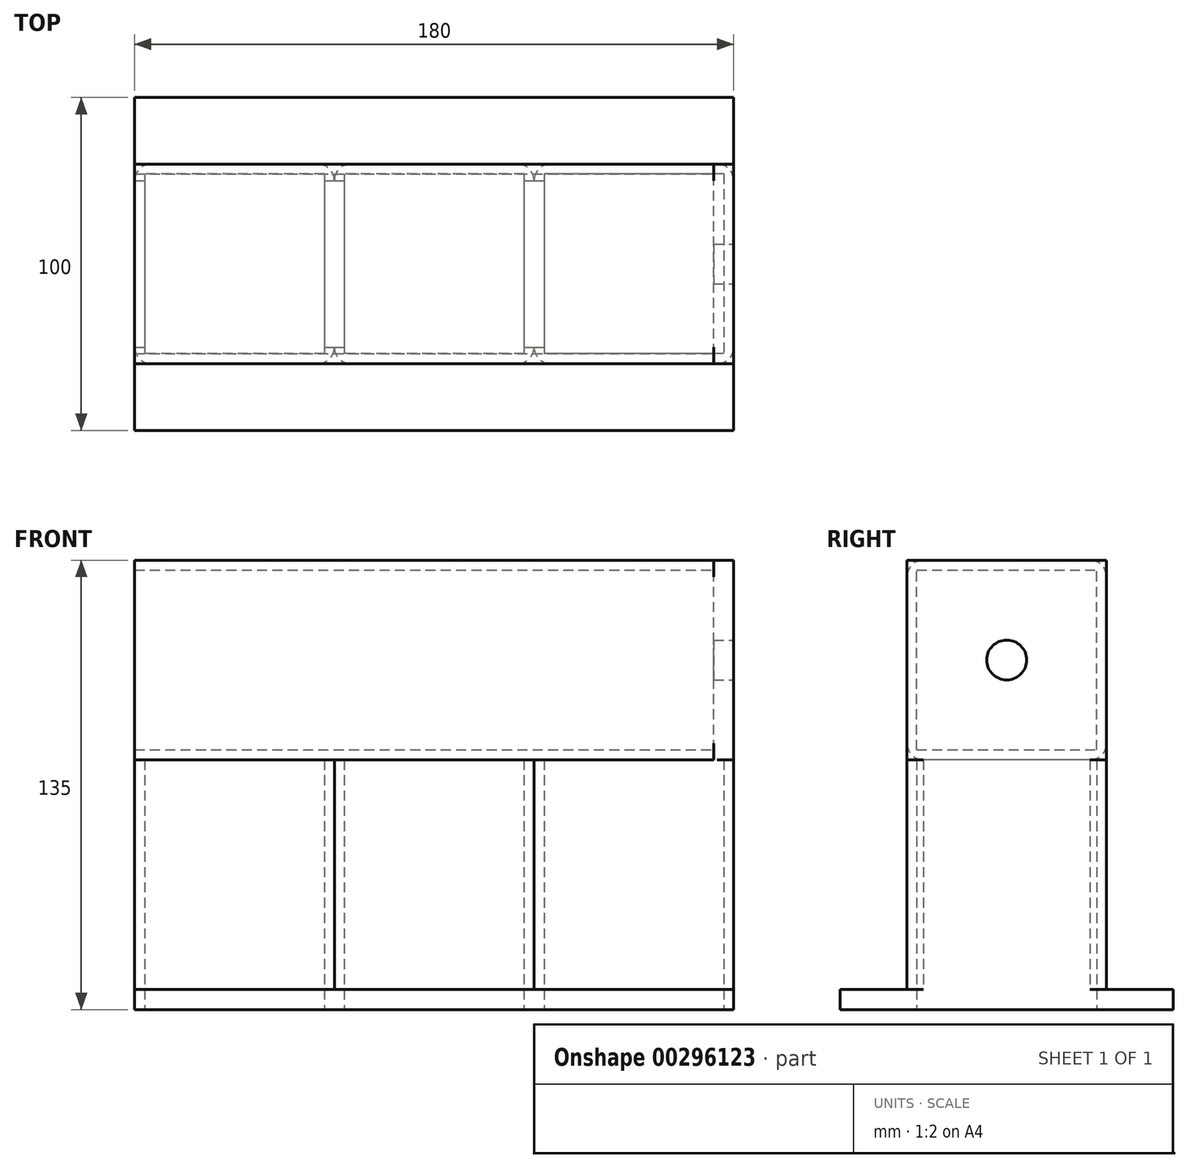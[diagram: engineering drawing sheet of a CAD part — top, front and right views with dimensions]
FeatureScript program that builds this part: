
annotation { "Feature Type Name" : "Feature", "Feature Type Description" : "" }
export const myFeature = defineFeature(function(context is Context, id is Id, definition is map)
    precondition{}
    {
        {
            var Q0;
            Q0=qCreatedBy(makeId("Top.planeOp"),FACE);
            var sketch = newSketch(context, id + "F0", { "sketchPlane" : qUnion([Q0])});
            skLineSegment(sketch, "E0.bottom", {"start": v(-15.85, -3.6) * mm, "end": v(-65.85, -3.6) * mm});
            skLineSegment(sketch, "E0.top", {"start": v(-15.85, -63.6) * mm, "end": v(-65.85, -63.6) * mm});
            skLineSegment(sketch, "E0.left", {"start": v(-10.85, -8.6) * mm, "end": v(-10.85, -58.6) * mm});
            skLineSegment(sketch, "E0.right", {"start": v(-70.85, -8.6) * mm, "end": v(-70.85, -58.6) * mm});
            skPoint(sketch, "E0.middle", {"position": v(-40.85, -33.6) * mm});
            skPoint(sketch, "E1.visualSharp", {"position": v(-70.85, -3.6) * mm});
            skArc(sketch, "E1.filletArc", {"start": v(-65.85, -3.6) * mm, "mid": v(-69.39, -5.06) * mm, "end": v(-70.85, -8.6) * mm});
            skPoint(sketch, "E2.visualSharp", {"position": v(-10.85, -3.6) * mm});
            skArc(sketch, "E2.filletArc", {"start": v(-10.85, -8.6) * mm, "mid": v(-12.31, -5.06) * mm, "end": v(-15.85, -3.6) * mm});
            skPoint(sketch, "E3.visualSharp", {"position": v(-10.85, -63.6) * mm});
            skArc(sketch, "E3.filletArc", {"start": v(-15.85, -63.6) * mm, "mid": v(-12.31, -62.13) * mm, "end": v(-10.85, -58.6) * mm});
            skPoint(sketch, "E4.visualSharp", {"position": v(-70.85, -63.6) * mm});
            skArc(sketch, "E4.filletArc", {"start": v(-70.85, -58.6) * mm, "mid": v(-69.39, -62.13) * mm, "end": v(-65.85, -63.6) * mm});
            skLineSegment(sketch, "E5.0", {"start": v(-67.85, -6.6) * mm, "end": v(-67.85, -60.6) * mm});
            skLineSegment(sketch, "E5.1", {"start": v(-13.85, -6.6) * mm, "end": v(-67.85, -6.6) * mm});
            skLineSegment(sketch, "E5.2", {"start": v(-13.85, -6.6) * mm, "end": v(-13.85, -60.6) * mm});
            skLineSegment(sketch, "E5.3", {"start": v(-13.85, -60.6) * mm, "end": v(-67.85, -60.6) * mm});
            skLineSegment(sketch, "E6.bottom", {"start": v(44.15, -3.6) * mm, "end": v(-5.85, -3.6) * mm});
            skLineSegment(sketch, "E6.top", {"start": v(44.15, -63.6) * mm, "end": v(-5.85, -63.6) * mm});
            skLineSegment(sketch, "E6.left", {"start": v(49.15, -8.6) * mm, "end": v(49.15, -58.6) * mm});
            skPoint(sketch, "E6.middle", {"position": v(19.15, -33.6) * mm});
            skArc(sketch, "E7.filletArc", {"start": v(-5.85, -3.6) * mm, "mid": v(-9.39, -5.06) * mm, "end": v(-10.85, -8.6) * mm});
            skPoint(sketch, "E8.visualSharp", {"position": v(49.15, -3.6) * mm});
            skArc(sketch, "E8.filletArc", {"start": v(49.15, -8.6) * mm, "mid": v(47.69, -5.06) * mm, "end": v(44.15, -3.6) * mm});
            skPoint(sketch, "E9.visualSharp", {"position": v(49.15, -63.6) * mm});
            skArc(sketch, "E9.filletArc", {"start": v(44.15, -63.6) * mm, "mid": v(47.69, -62.13) * mm, "end": v(49.15, -58.6) * mm});
            skArc(sketch, "E10.filletArc", {"start": v(-10.85, -58.6) * mm, "mid": v(-9.39, -62.13) * mm, "end": v(-5.85, -63.6) * mm});
            skLineSegment(sketch, "E11.0", {"start": v(-7.85, -6.6) * mm, "end": v(-7.85, -60.6) * mm});
            skLineSegment(sketch, "E11.1", {"start": v(46.15, -6.6) * mm, "end": v(-7.85, -6.6) * mm});
            skLineSegment(sketch, "E11.2", {"start": v(46.15, -6.6) * mm, "end": v(46.15, -60.6) * mm});
            skLineSegment(sketch, "E11.3", {"start": v(46.15, -60.6) * mm, "end": v(-7.85, -60.6) * mm});
            skLineSegment(sketch, "E12.bottom", {"start": v(104.15, -3.6) * mm, "end": v(54.15, -3.6) * mm});
            skLineSegment(sketch, "E12.top", {"start": v(104.15, -63.6) * mm, "end": v(54.15, -63.6) * mm});
            skLineSegment(sketch, "E12.left", {"start": v(109.15, -8.6) * mm, "end": v(109.15, -58.6) * mm});
            skPoint(sketch, "E12.middle", {"position": v(79.15, -33.6) * mm});
            skArc(sketch, "E13.filletArc", {"start": v(54.15, -3.6) * mm, "mid": v(50.61, -5.06) * mm, "end": v(49.15, -8.6) * mm});
            skPoint(sketch, "E14.visualSharp", {"position": v(109.15, -3.6) * mm});
            skArc(sketch, "E14.filletArc", {"start": v(109.15, -8.6) * mm, "mid": v(107.69, -5.06) * mm, "end": v(104.15, -3.6) * mm});
            skPoint(sketch, "E15.visualSharp", {"position": v(109.15, -63.6) * mm});
            skArc(sketch, "E15.filletArc", {"start": v(104.15, -63.6) * mm, "mid": v(107.69, -62.13) * mm, "end": v(109.15, -58.6) * mm});
            skArc(sketch, "E16.filletArc", {"start": v(49.15, -58.6) * mm, "mid": v(50.61, -62.13) * mm, "end": v(54.15, -63.6) * mm});
            skLineSegment(sketch, "E17.0", {"start": v(52.15, -6.6) * mm, "end": v(52.15, -60.6) * mm});
            skLineSegment(sketch, "E17.1", {"start": v(106.15, -6.6) * mm, "end": v(52.15, -6.6) * mm});
            skLineSegment(sketch, "E17.2", {"start": v(106.15, -6.6) * mm, "end": v(106.15, -60.6) * mm});
            skLineSegment(sketch, "E17.3", {"start": v(106.15, -60.6) * mm, "end": v(52.15, -60.6) * mm});
            skSolve(sketch);
        }
        {
            var Q0;
            Q0=makeQuery(id+"F0.imprint","IMPRINT",FACE,{"disambiguationData":[TD([[makeQuery(id+"F0.imprint","IMPRINT",EDGE,{"derivedFrom":sQuery(id+"F0.wireOp",EDGE,"E0.bottom")}),1.0]])]});
            var Q1;
            Q1=makeQuery(id+"F0.imprint","IMPRINT",FACE,{"disambiguationData":[TD([[makeQuery(id+"F0.imprint","IMPRINT",EDGE,{"derivedFrom":sQuery(id+"F0.wireOp",EDGE,"E6.bottom")}),1.0]])]});
            var Q2;
            Q2=makeQuery(id+"F0.imprint","IMPRINT",FACE,{"disambiguationData":[TD([[makeQuery(id+"F0.imprint","IMPRINT",EDGE,{"derivedFrom":sQuery(id+"F0.wireOp",EDGE,"E12.bottom")}),1.0]])]});
            extrude(context, id + "F1", {"entities" : qUnion([Q0, Q1, Q2]), "depth" : 69 * mm});
        }
        {
            var Q0;
            Q0=makeQuery(id+"F1.opExtrude","CAP_FACE",FACE,{"disambiguationData":[OSD([sQuery(id+"F0.wireOp",EDGE,"E0.bottom"),sQuery(id+"F0.wireOp",EDGE,"E0.top"),sQuery(id+"F0.wireOp",EDGE,"E0.right"),sQuery(id+"F0.wireOp",EDGE,"E1.filletArc"),sQuery(id+"F0.wireOp",EDGE,"E2.filletArc"),sQuery(id+"F0.wireOp",EDGE,"E3.filletArc"),sQuery(id+"F0.wireOp",EDGE,"E4.filletArc"),sQuery(id+"F0.wireOp",EDGE,"E5.0"),sQuery(id+"F0.wireOp",EDGE,"E5.1"),sQuery(id+"F0.wireOp",EDGE,"E5.2"),sQuery(id+"F0.wireOp",EDGE,"E5.3"),sQuery(id+"F0.wireOp",EDGE,"E6.bottom"),sQuery(id+"F0.wireOp",EDGE,"E6.top"),sQuery(id+"F0.wireOp",EDGE,"E7.filletArc"),sQuery(id+"F0.wireOp",EDGE,"E8.filletArc"),sQuery(id+"F0.wireOp",EDGE,"E9.filletArc"),sQuery(id+"F0.wireOp",EDGE,"E10.filletArc"),sQuery(id+"F0.wireOp",EDGE,"E11.0"),sQuery(id+"F0.wireOp",EDGE,"E11.1"),sQuery(id+"F0.wireOp",EDGE,"E11.2"),sQuery(id+"F0.wireOp",EDGE,"E11.3"),sQuery(id+"F0.wireOp",EDGE,"E12.bottom"),sQuery(id+"F0.wireOp",EDGE,"E12.top"),sQuery(id+"F0.wireOp",EDGE,"E12.left"),sQuery(id+"F0.wireOp",EDGE,"E13.filletArc"),sQuery(id+"F0.wireOp",EDGE,"E14.filletArc"),sQuery(id+"F0.wireOp",EDGE,"E15.filletArc"),sQuery(id+"F0.wireOp",EDGE,"E16.filletArc"),sQuery(id+"F0.wireOp",EDGE,"E17.0"),sQuery(id+"F0.wireOp",EDGE,"E17.1"),sQuery(id+"F0.wireOp",EDGE,"E17.2"),sQuery(id+"F0.wireOp",EDGE,"E17.3")])],"isStart":true});
            var sketch = newSketch(context, id + "F2", { "sketchPlane" : qUnion([Q0])});
            skLineSegment(sketch, "E18.bottom", {"start": v(109.15, -16.4) * mm, "end": v(-70.85, -16.4) * mm});
            skLineSegment(sketch, "E18.top", {"start": v(109.15, 83.6) * mm, "end": v(-70.85, 83.6) * mm});
            skLineSegment(sketch, "E18.left", {"start": v(109.15, -16.4) * mm, "end": v(109.15, 83.6) * mm});
            skLineSegment(sketch, "E18.right", {"start": v(-70.85, -16.4) * mm, "end": v(-70.85, 83.6) * mm});
            skSolve(sketch);
        }
        {
            var Q0;
            {var subQ2=sQuery(id+"F2.wireOp",EDGE,"E18.bottom");Q0=makeQuery(id+"F2.imprint","IMPRINT",FACE,{"disambiguationData":[TD([[makeQuery(id+"F2.imprint","IMPRINT",EDGE,{"derivedFrom":subQ2}),-1.0]])]});}
            var Q1;
            {var subQ1=sQuery(id+"F2.wireOp",EDGE,"E18.top");Q1=makeQuery(id+"F2.imprint","IMPRINT",FACE,{"disambiguationData":[TD([[makeQuery(id+"F2.imprint","IMPRINT",EDGE,{"derivedFrom":subQ1}),1.0]])]});}
            var Q2;
            Q2=makeQuery(id+"F2.imprint","IMPRINT",FACE,{"disambiguationData":[TD([[makeQuery(id+"F2.imprint","IMPRINT",EDGE,{"derivedFrom":makeQuery(id+"F1.opExtrude","CAP_EDGE",EDGE,{"disambiguationData":[OSD([sQuery(id+"F0.wireOp",EDGE,"E0.bottom")])],"isStart":true})}),-1.0]])]});
            extrude(context, id + "F3", {"entities" : qUnion([Q0, Q1, Q2]), "operationType" : NewBodyOperationType.ADD, "depth" : 6 * mm});
        }
        {
            var Q0;
            Q0=makeQuery(id+"F3.boolean.opBoolean","MERGE",FACE,{"derivedFrom":[makeQuery(id+"F1.opExtrude","SWEPT_FACE",FACE,{"disambiguationData":[OSD([sQuery(id+"F0.wireOp",EDGE,"E12.left")])]}),makeQuery(id+"F3.opExtrude","SWEPT_FACE",FACE,{"disambiguationData":[OSD([sQuery(id+"F2.wireOp",EDGE,"E18.left")])]})]});
            var sketch = newSketch(context, id + "F4", { "sketchPlane" : qUnion([Q0])});
            skLineSegment(sketch, "E19.bottom", {"start": v(-8.6, 129) * mm, "end": v(-58.6, 129) * mm});
            skLineSegment(sketch, "E19.top", {"start": v(-8.6, 69) * mm, "end": v(-58.6, 69) * mm});
            skLineSegment(sketch, "E19.left", {"start": v(-3.6, 124) * mm, "end": v(-3.6, 74) * mm});
            skLineSegment(sketch, "E19.right", {"start": v(-63.6, 124) * mm, "end": v(-63.6, 74) * mm});
            skPoint(sketch, "E19.middle", {"position": v(-33.6, 99) * mm});
            skPoint(sketch, "E20.visualSharp", {"position": v(-63.6, 129) * mm});
            skArc(sketch, "E20.filletArc", {"start": v(-58.6, 129) * mm, "mid": v(-62.13, 127.54) * mm, "end": v(-63.6, 124) * mm});
            skPoint(sketch, "E21.visualSharp", {"position": v(-3.6, 129) * mm});
            skArc(sketch, "E21.filletArc", {"start": v(-3.6, 124) * mm, "mid": v(-5.06, 127.54) * mm, "end": v(-8.6, 129) * mm});
            skPoint(sketch, "E22.visualSharp", {"position": v(-3.6, 69) * mm});
            skArc(sketch, "E22.filletArc", {"start": v(-8.6, 69) * mm, "mid": v(-5.06, 70.46) * mm, "end": v(-3.6, 74) * mm});
            skPoint(sketch, "E23.visualSharp", {"position": v(-63.6, 69) * mm});
            skArc(sketch, "E23.filletArc", {"start": v(-63.6, 74) * mm, "mid": v(-62.13, 70.46) * mm, "end": v(-58.6, 69) * mm});
            skLineSegment(sketch, "E24.0", {"start": v(-60.6, 126) * mm, "end": v(-60.6, 72) * mm});
            skLineSegment(sketch, "E24.1", {"start": v(-6.6, 126) * mm, "end": v(-60.6, 126) * mm});
            skLineSegment(sketch, "E24.2", {"start": v(-6.6, 126) * mm, "end": v(-6.6, 72) * mm});
            skLineSegment(sketch, "E24.3", {"start": v(-6.6, 72) * mm, "end": v(-60.6, 72) * mm});
            skSolve(sketch);
        }
        {
            var Q0;
            Q0=makeQuery(id+"F4.imprint","IMPRINT",FACE,{"disambiguationData":[TD([[makeQuery(id+"F4.imprint","IMPRINT",EDGE,{"derivedFrom":sQuery(id+"F4.wireOp",EDGE,"E19.bottom")}),1.0]])]});
            var Q1;
            Q1=makeQuery(id+"F3.boolean.opBoolean","MERGE",FACE,{"derivedFrom":[makeQuery(id+"F1.opExtrude","SWEPT_FACE",FACE,{"disambiguationData":[OSD([sQuery(id+"F0.wireOp",EDGE,"E0.right")])]}),makeQuery(id+"F3.opExtrude","SWEPT_FACE",FACE,{"disambiguationData":[OSD([sQuery(id+"F2.wireOp",EDGE,"E18.right")])]})]});
            extrude(context, id + "F5", {"entities" : qUnion([Q0]), "operationType" : NewBodyOperationType.ADD, "endBound" : BoundingType.UP_TO_SURFACE, "oppositeDirection" : true, "endBoundEntityFace" : qUnion([Q1]), "depth" : 25 * mm});
        }
        {
            var Q0;
            Q0=makeQuery(id+"F5.boolean.opBoolean","MERGE",FACE,{"derivedFrom":[makeQuery(id+"F3.boolean.opBoolean","MERGE",FACE,{"derivedFrom":[makeQuery(id+"F1.opExtrude","SWEPT_FACE",FACE,{"disambiguationData":[OSD([sQuery(id+"F0.wireOp",EDGE,"E12.left")])]}),makeQuery(id+"F3.opExtrude","SWEPT_FACE",FACE,{"disambiguationData":[OSD([sQuery(id+"F2.wireOp",EDGE,"E18.left")])]})]}),makeQuery(id+"F5.opExtrude","CAP_FACE",FACE,{"disambiguationData":[OSD([sQuery(id+"F4.wireOp",EDGE,"E19.bottom"),sQuery(id+"F4.wireOp",EDGE,"E19.top"),sQuery(id+"F4.wireOp",EDGE,"E19.left"),sQuery(id+"F4.wireOp",EDGE,"E19.right"),sQuery(id+"F4.wireOp",EDGE,"E20.filletArc"),sQuery(id+"F4.wireOp",EDGE,"E21.filletArc"),sQuery(id+"F4.wireOp",EDGE,"E22.filletArc"),sQuery(id+"F4.wireOp",EDGE,"E23.filletArc"),sQuery(id+"F4.wireOp",EDGE,"E24.0"),sQuery(id+"F4.wireOp",EDGE,"E24.1"),sQuery(id+"F4.wireOp",EDGE,"E24.2"),sQuery(id+"F4.wireOp",EDGE,"E24.3")])],"isStart":true})]});
            var sketch = newSketch(context, id + "F6", { "sketchPlane" : qUnion([Q0])});
            skLineSegment(sketch, "E25.bottom", {"start": v(-3.6, 129) * mm, "end": v(-63.6, 129) * mm});
            skLineSegment(sketch, "E25.top", {"start": v(-3.6, 69) * mm, "end": v(-63.6, 69) * mm});
            skLineSegment(sketch, "E25.left", {"start": v(-3.6, 129) * mm, "end": v(-3.6, 69) * mm});
            skLineSegment(sketch, "E25.right", {"start": v(-63.6, 129) * mm, "end": v(-63.6, 69) * mm});
            skCircle(sketch, "E26", {"center": v(-33.6, 99) * mm, "radius": 6 * mm});
            skSolve(sketch);
        }
        {
            var Q0;
            Q0=qSketchRegion(id+"F6",true);
            extrude(context, id + "F7", {"entities" : qUnion([Q0]), "operationType" : NewBodyOperationType.ADD, "oppositeDirection" : true, "depth" : 6 * mm});
        }
    });
